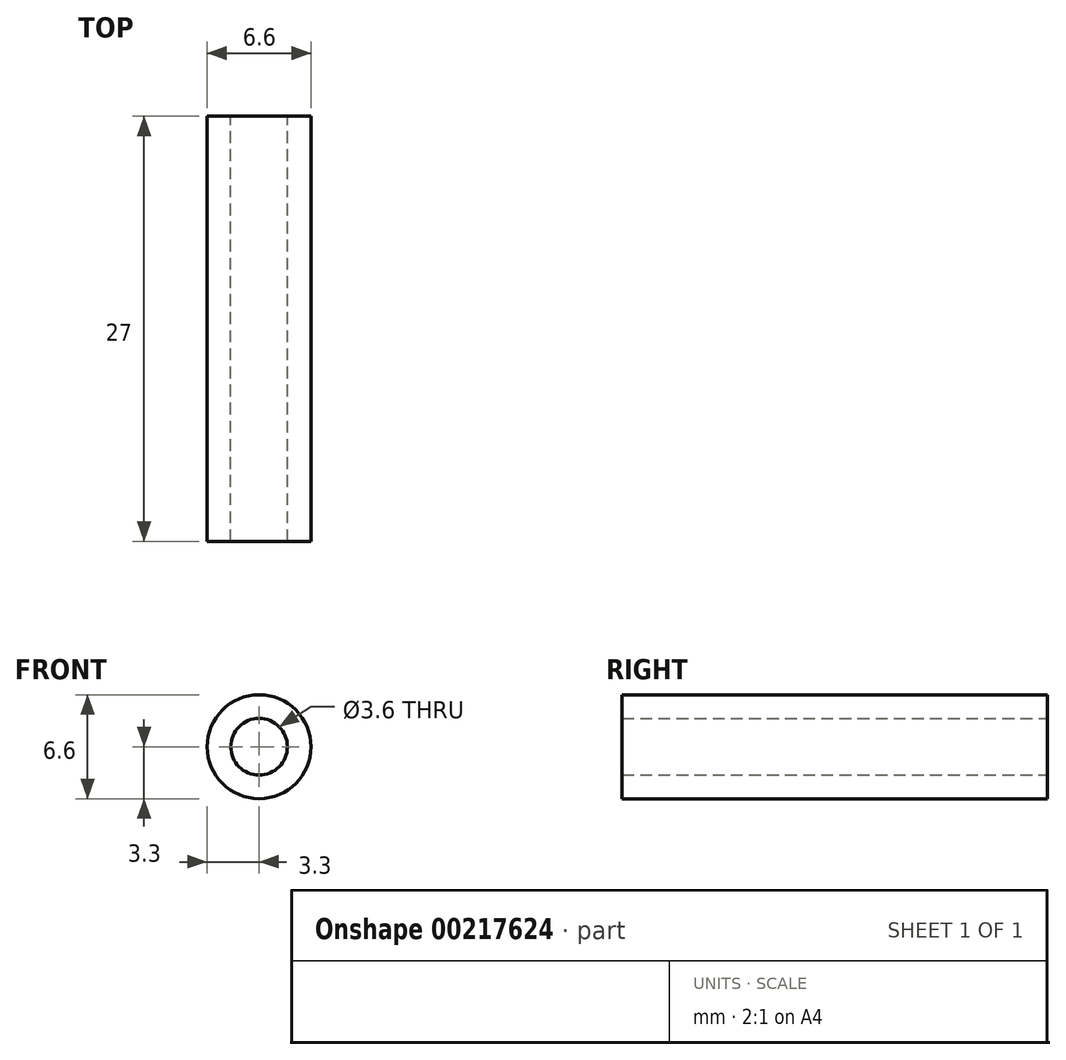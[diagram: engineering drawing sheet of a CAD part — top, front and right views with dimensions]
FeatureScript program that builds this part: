
annotation { "Feature Type Name" : "Feature", "Feature Type Description" : "" }
export const myFeature = defineFeature(function(context is Context, id is Id, definition is map)
    precondition{}
    {
        {
            var Q0;
            Q0=qCreatedBy(makeId("Right.planeOp"),FACE);
            var sketch = newSketch(context, id + "F0", { "sketchPlane" : qUnion([Q0])});
            skLineSegment(sketch, "E0", {"start": v(0, 0) * mm, "end": v(-21.48, 0) * mm, "construction": true});
            skLineSegment(sketch, "E1.bottom", {"start": v(0, 1.8) * mm, "end": v(-27, 1.8) * mm});
            skLineSegment(sketch, "E1.top", {"start": v(0, 3.3) * mm, "end": v(-27, 3.3) * mm});
            skLineSegment(sketch, "E1.left", {"start": v(0, 1.8) * mm, "end": v(0, 3.3) * mm});
            skLineSegment(sketch, "E1.right", {"start": v(-27, 1.8) * mm, "end": v(-27, 3.3) * mm});
            skSolve(sketch);
        }
        {
            var Q0;
            Q0 = qSketchRegion(id + "F0", true);
            var Q1;
            Q1=sQuery(id+"F0.wireOp",EDGE,"E0");
            revolve(context, id + "F1", {"entities" : qUnion([Q0]), "axis" : qUnion([Q1]), "revolveType" : RevolveType.FULL});
        }
    });
